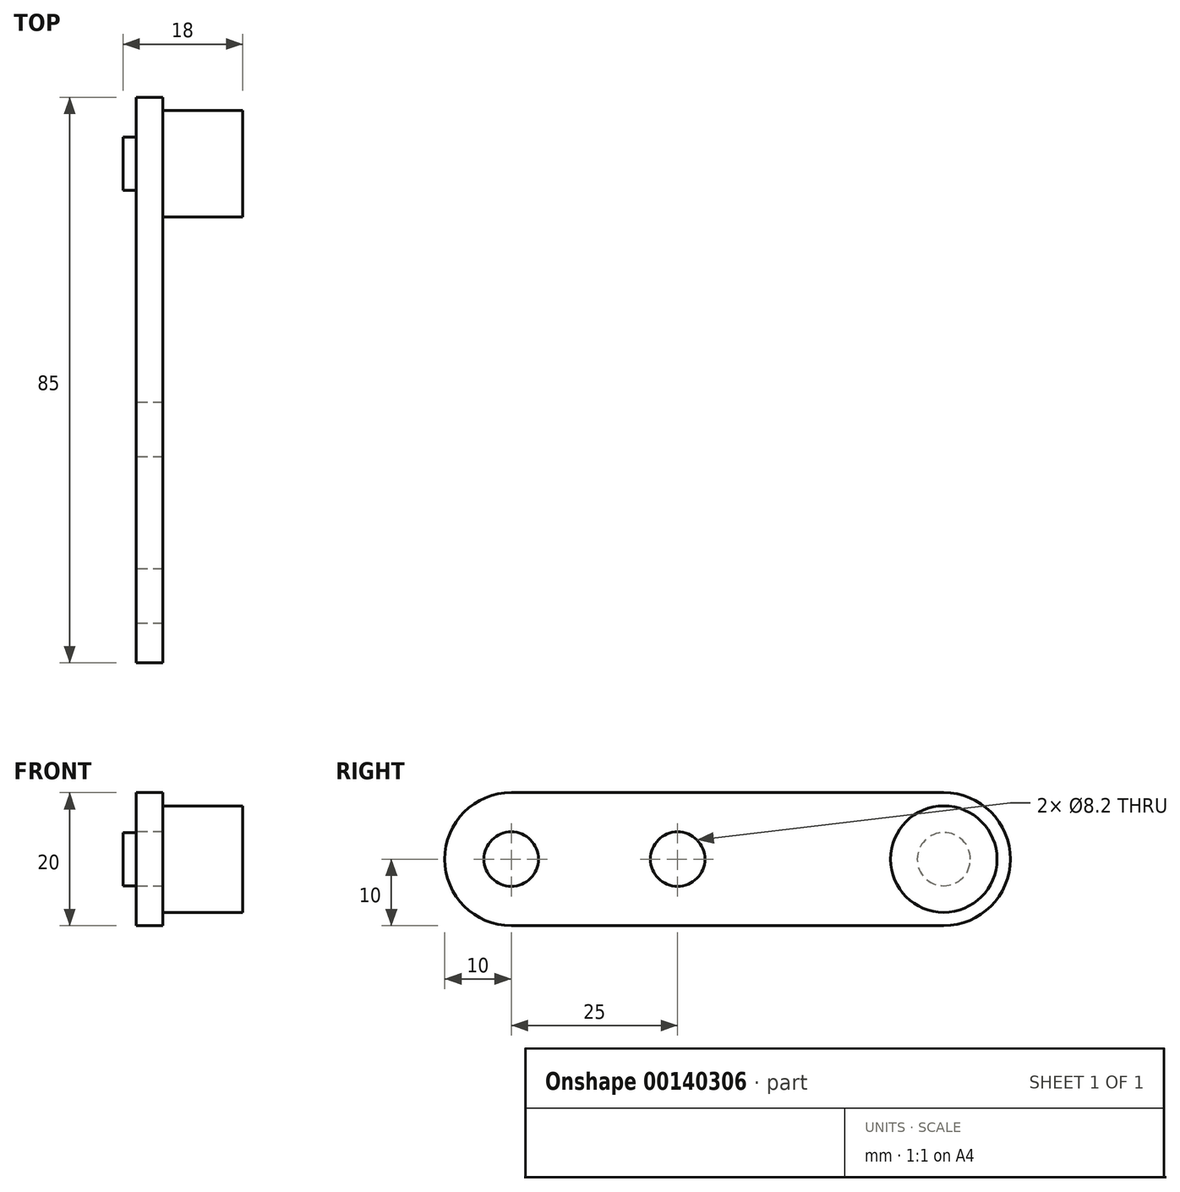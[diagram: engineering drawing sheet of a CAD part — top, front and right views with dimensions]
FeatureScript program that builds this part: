
annotation { "Feature Type Name" : "Feature", "Feature Type Description" : "" }
export const myFeature = defineFeature(function(context is Context, id is Id, definition is map)
    precondition{}
    {
        {
            var Q0;
            Q0=qCreatedBy(makeId("Right.planeOp"),FACE);
            var sketch = newSketch(context, id + "F0", { "sketchPlane" : qUnion([Q0])});
            skCircle(sketch, "E0", {"center": v(0, 0) * mm, "radius": 4.1 * mm});
            skArc(sketch, "E1", {"start": v(0, 10) * mm, "mid": v(-10, 0) * mm, "end": v(0, -10) * mm});
            skArc(sketch, "E2", {"start": v(65, -10) * mm, "mid": v(75, 0) * mm, "end": v(65, 10) * mm});
            skLineSegment(sketch, "E3", {"start": v(0, 10) * mm, "end": v(65, 10) * mm});
            skLineSegment(sketch, "E4", {"start": v(0, -10) * mm, "end": v(65, -10) * mm});
            skCircle(sketch, "E5", {"center": v(25, 0) * mm, "radius": 4.1 * mm});
            skSolve(sketch);
        }
        {
            var Q0;
            Q0=makeQuery(id+"F0.imprint","IMPRINT",FACE,{"disambiguationData":[TD([[makeQuery(id+"F0.imprint","IMPRINT",EDGE,{"derivedFrom":sQuery(id+"F0.wireOp",EDGE,"E0")}),-1.0]])]});
            extrude(context, id + "F1", {"entities" : qUnion([Q0]), "depth" : 4 * mm});
        }
        {
            var Q0;
            Q0=qCreatedBy(makeId("Right.planeOp"),FACE);
            var sketch = newSketch(context, id + "F2", { "sketchPlane" : qUnion([Q0])});
            skCircle(sketch, "E6", {"center": v(65, 0) * mm, "radius": 8 * mm});
            skCircle(sketch, "E7", {"center": v(65, 0) * mm, "radius": 4 * mm});
            skSolve(sketch);
        }
        {
            var Q0;
            Q0=makeQuery(id+"F2.imprint","IMPRINT",FACE,{"disambiguationData":[TD([[makeQuery(id+"F2.imprint","IMPRINT",EDGE,{"derivedFrom":sQuery(id+"F2.wireOp",EDGE,"E6")}),1.0]])]});
            var Q1;
            Q1=makeQuery(id+"F2.imprint","IMPRINT",FACE,{"disambiguationData":[TD([[makeQuery(id+"F2.imprint","IMPRINT",EDGE,{"derivedFrom":sQuery(id+"F2.wireOp",EDGE,"E7")}),1.0]])]});
            extrude(context, id + "F3", {"entities" : qUnion([Q0, Q1]), "operationType" : NewBodyOperationType.ADD, "depth" : 16 * mm});
        }
        {
            var Q0;
            Q0=makeQuery(id+"F2.imprint","IMPRINT",FACE,{"disambiguationData":[TD([[makeQuery(id+"F2.imprint","IMPRINT",EDGE,{"derivedFrom":sQuery(id+"F2.wireOp",EDGE,"E7")}),1.0]])]});
            extrude(context, id + "F4", {"entities" : qUnion([Q0]), "operationType" : NewBodyOperationType.ADD, "oppositeDirection" : true, "depth" : 2 * mm});
        }
    });
